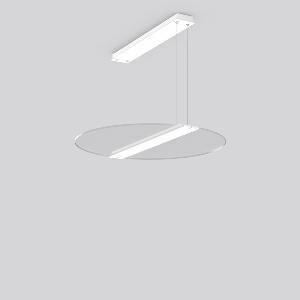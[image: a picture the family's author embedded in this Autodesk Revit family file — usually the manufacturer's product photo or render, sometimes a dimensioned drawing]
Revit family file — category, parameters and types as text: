
# Revit family: twindot_s_round_312353_002_d7c7
name_source: partatom
category: Lighting Fixtures
units: mm (PartAtom-declared; Revit-internal decimal feet)

## family parameters
Cut with Voids When Loaded = No
Host = Face
Light Source = No
Part Type = Normal
Room Calculation Point = No
Round Connector Dimension = Use Diameter
Shared = No

## types (1)
- TWINDOT S round (1 x LED Modul 830, 4500 lm, 3000)
    Apparent Load = 41 VA
    CIE Flux Codes = 49 78 94 56 100
    Color Rendering = 80
    Color Temperature = 3000
    Default Elevation = 1800 mm
    Description = Series: TWINDOT S round
LED pendant luminaire with extremely flat and frameless appearance. Middle bar made of aluminium extrusion profile, powder-coated. Transparent light guide made of UV-resistant acrylic glass (PMMA) with TWINDOT prismatic. Light control with perfectly glare-free TWINDOT technology for pleasantly gentle light with soft shadows. Even and wide indirect and direct light distribution. Direct 55%, indirect 45% light emission. 4-point steel cable suspension, steplessly adjustable. Converter integrated in the canopy (powder-coated white). Power supply through suspension cable. 
Colour: traffic white, matt (RAL 9016)
Diameter: 645 mm
Height: 20 mm
Suspension length: 500-1200 mm
Lamp: LED
Socket: without socket
Colour temperature: 3000K
Colour rendering index (CRI): 80
System power: 41 W
Rated luminous flux: 4500 lm
Luminous efficiency: 110 lm/W
Control gear: Regulated power supply
Protection class: I
Type of protection: IP 20
    Height = 20 mm  [stored 0.0656168 ft]
    Lamp = 1 x LED Modul 830
    Lamp Light Flux = 4500 lm
    Lamp count = 1
    Length = 645 mm
    Lifetime = 50000 h
    Luminous efficacy = 110 lm/W
    Manufacturer = RZB
    ModVariant = No
    Model = 312353.002
    Mounting Place = Ceiling
    Mounting Type = Pendant
    Number of Poles = 1
    OnlyDefault = Yes
    Power Factor = 1
    Product Name = TWINDOT S round
    Product group = Pendant modular luminaires
    ProductGroupID = 906
    Protection Class = Protection class I
    Protection Degree = IP 20
    RLX_Detail_Level = 1
    RLX_Emergency_Light_Flux = 0 lm
    RLX_Emergency_Type = 0
    RLX_Emergency_Type_DB = No
    RlxData = <blob elided: 36149 chars, md5=0503310d>
    Socket = socket
    Standby Power = 0 W
    System Light Flux = 4500 lm
    System Power = 41 W
    Type Comments = Product without accessories
    Type Image = 312353.002.jpg
    URL = http://relux.com
    VarID = ---
    Voltage = 230 V
    Voltage Range = 220-240 V
    Weight = 0.00 kg
    Width = 0 mm  [stored 0 ft]

note: [stored X ft] marks values corroborated as IEEE doubles in the binary element streams (Revit-internal decimal feet)

## geometry (parser evidence)
native form markers: Blend x4, Sweep x12
no freeform markers — native parametric forms only
